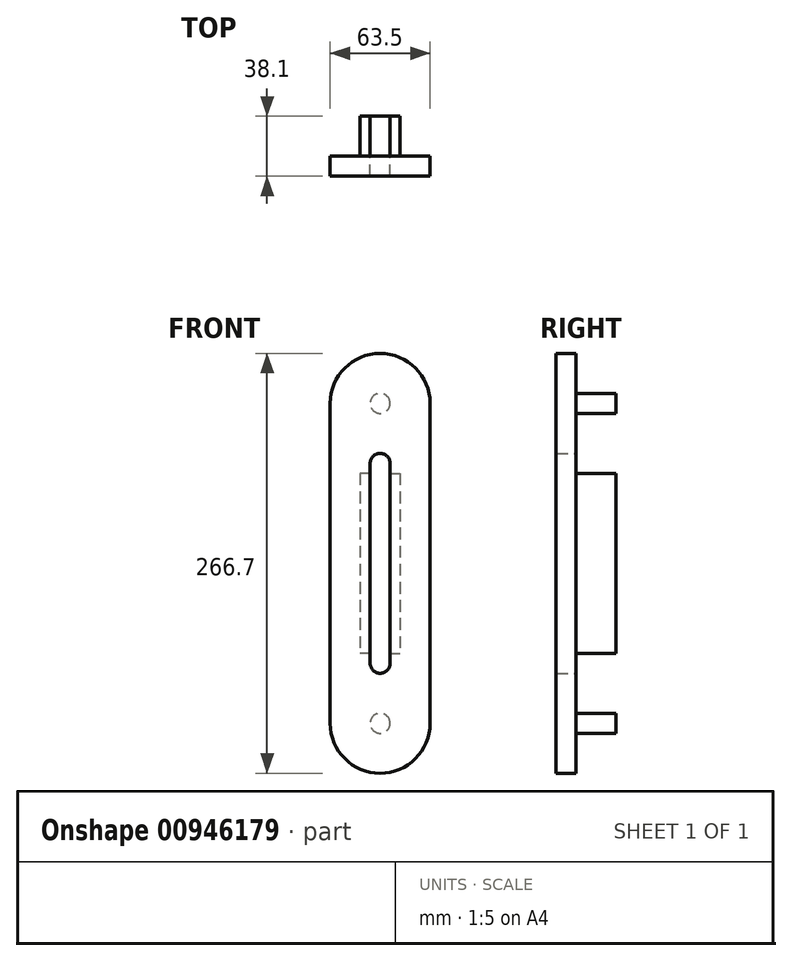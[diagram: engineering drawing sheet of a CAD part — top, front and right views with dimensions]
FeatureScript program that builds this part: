
annotation { "Feature Type Name" : "Feature", "Feature Type Description" : "" }
export const myFeature = defineFeature(function(context is Context, id is Id, definition is map)
    precondition{}
    {
        {
            var Q0;
            Q0=qCreatedBy(makeId("Front.planeOp"),FACE);
            var sketch = newSketch(context, id + "F0", { "sketchPlane" : qUnion([Q0])});
            skCircle(sketch, "E0", {"center": v(3.93, 25.3) * mm, "radius": 6.35 * mm});
            skCircle(sketch, "E1", {"center": v(3.93, -177.9) * mm, "radius": 6.35 * mm});
            skSolve(sketch);
        }
        {
            var Q0;
            Q0 = qSketchRegion(id + "F0", true);
            extrude(context, id + "F1", {"entities" : qUnion([Q0]), "depth" : 25.4 * mm, "offsetDistance" : 25.4 * mm});
        }
        {
            var Q0;
            Q0=makeQuery(id+"F1.opExtrude","CAP_FACE",FACE,{"disambiguationData":[OSD([sQuery(id+"F0.wireOp",EDGE,"E0")])],"isStart":false});
            var sketch = newSketch(context, id + "F2", { "sketchPlane" : qUnion([Q0])});
            skLineSegment(sketch, "E2.left", {"start": v(-27.82, 25.3) * mm, "end": v(-27.82, -177.9) * mm});
            skPoint(sketch, "E3.visualSharp", {"position": v(-27.82, 57.05) * mm});
            skArc(sketch, "E3.filletArc", {"start": v(3.93, 57.05) * mm, "mid": v(-18.52, 47.75) * mm, "end": v(-27.82, 25.3) * mm});
            skPoint(sketch, "E4.visualSharp", {"position": v(35.68, 57.05) * mm});
            skArc(sketch, "E4.filletArc", {"start": v(35.68, 25.3) * mm, "mid": v(26.38, 47.75) * mm, "end": v(3.93, 57.05) * mm});
            skPoint(sketch, "E5.visualSharp", {"position": v(-27.82, -209.65) * mm});
            skArc(sketch, "E5.filletArc", {"start": v(-27.82, -177.9) * mm, "mid": v(-18.52, -200.35) * mm, "end": v(3.93, -209.65) * mm});
            skPoint(sketch, "E6.visualSharp", {"position": v(35.68, -209.65) * mm});
            skArc(sketch, "E6.filletArc", {"start": v(3.93, -209.65) * mm, "mid": v(26.38, -200.35) * mm, "end": v(35.68, -177.9) * mm});
            skLineSegment(sketch, "E7", {"start": v(35.68, 25.3) * mm, "end": v(35.68, -177.9) * mm});
            skLineSegment(sketch, "E8.bottom", {"start": v(3.93, -6.45) * mm, "end": v(3.93, -6.45) * mm});
            skLineSegment(sketch, "E8.top", {"start": v(3.93, -146.15) * mm, "end": v(3.93, -146.15) * mm});
            skLineSegment(sketch, "E8.left", {"start": v(10.28, -12.8) * mm, "end": v(10.28, -139.8) * mm});
            skLineSegment(sketch, "E8.right", {"start": v(-2.42, -12.8) * mm, "end": v(-2.42, -139.8) * mm});
            skPoint(sketch, "E9.visualSharp", {"position": v(10.28, -6.45) * mm});
            skArc(sketch, "E9.filletArc", {"start": v(10.28, -12.8) * mm, "mid": v(8.42, -8.3) * mm, "end": v(3.93, -6.45) * mm});
            skPoint(sketch, "E10.visualSharp", {"position": v(-2.42, -6.45) * mm});
            skArc(sketch, "E10.filletArc", {"start": v(3.93, -6.45) * mm, "mid": v(-0.56, -8.3) * mm, "end": v(-2.42, -12.8) * mm});
            skPoint(sketch, "E11.visualSharp", {"position": v(-2.42, -146.15) * mm});
            skArc(sketch, "E11.filletArc", {"start": v(-2.42, -139.8) * mm, "mid": v(-0.56, -144.29) * mm, "end": v(3.93, -146.15) * mm});
            skPoint(sketch, "E12.visualSharp", {"position": v(10.28, -146.15) * mm});
            skArc(sketch, "E12.filletArc", {"start": v(3.93, -146.15) * mm, "mid": v(8.42, -144.29) * mm, "end": v(10.28, -139.8) * mm});
            skSolve(sketch);
        }
        {
            var Q0;
            Q0 = qSketchRegion(id + "F2", true);
            extrude(context, id + "F3", {"entities" : qUnion([Q0]), "depth" : 12.7 * mm, "offsetDistance" : 25.4 * mm});
        }
        {
            var Q0;
            Q0=makeQuery(id+"F3.opExtrude","CAP_FACE",FACE,{"disambiguationData":[OSD([sQuery(id+"F2.wireOp",EDGE,"E2.left"),sQuery(id+"F2.wireOp",EDGE,"E3.filletArc"),sQuery(id+"F2.wireOp",EDGE,"E4.filletArc"),sQuery(id+"F2.wireOp",EDGE,"E5.filletArc"),sQuery(id+"F2.wireOp",EDGE,"E6.filletArc"),sQuery(id+"F2.wireOp",EDGE,"E7"),sQuery(id+"F2.wireOp",EDGE,"E8.left"),sQuery(id+"F2.wireOp",EDGE,"E8.right"),sQuery(id+"F2.wireOp",EDGE,"E9.filletArc"),sQuery(id+"F2.wireOp",EDGE,"E10.filletArc"),sQuery(id+"F2.wireOp",EDGE,"E11.filletArc"),sQuery(id+"F2.wireOp",EDGE,"E12.filletArc")])],"isStart":true});
            var sketch = newSketch(context, id + "F4", { "sketchPlane" : qUnion([Q0])});
            skLineSegment(sketch, "E13.bottom", {"start": v(2.42, -19.15) * mm, "end": v(8.77, -19.15) * mm});
            skLineSegment(sketch, "E13.top", {"start": v(2.42, -133.45) * mm, "end": v(8.77, -133.45) * mm});
            skLineSegment(sketch, "E13.left", {"start": v(2.42, -19.15) * mm, "end": v(2.42, -133.45) * mm});
            skLineSegment(sketch, "E13.right", {"start": v(8.77, -19.15) * mm, "end": v(8.77, -133.45) * mm});
            skLineSegment(sketch, "E14.bottom", {"start": v(-10.28, -19.15) * mm, "end": v(-16.63, -19.15) * mm});
            skLineSegment(sketch, "E14.top", {"start": v(-10.28, -133.45) * mm, "end": v(-16.63, -133.45) * mm});
            skLineSegment(sketch, "E14.left", {"start": v(-10.28, -19.15) * mm, "end": v(-10.28, -133.45) * mm});
            skLineSegment(sketch, "E14.right", {"start": v(-16.63, -19.15) * mm, "end": v(-16.63, -133.45) * mm});
            skSolve(sketch);
        }
        {
            var Q0;
            Q0 = qSketchRegion(id + "F4", true);
            extrude(context, id + "F5", {"entities" : qUnion([Q0]), "operationType" : NewBodyOperationType.ADD, "depth" : 25.4 * mm, "offsetDistance" : 25.4 * mm});
        }
    });
